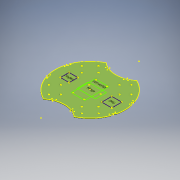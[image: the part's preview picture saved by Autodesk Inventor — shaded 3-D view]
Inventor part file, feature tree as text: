
AUTODESK INVENTOR PART (.ipt)
format: ipt  version: 2020 (Build 240168000, 168)  size: 317,952 bytes
history: native  units: mm
features: sketch x7, other x4, hole x4, extrude x2, fillet x1, projected_geometry x1
ambient origin geometry x8: Origin, YZ Plane, XZ Plane, XY Plane, X Axis, Y Axis, Z Axis, Center Point
bodies: Body1 (feature_tree)
feature tree (19):
  other  "motherboard"
  other  "contour"
  other  "Твердое тело1"
  extrude  "Выдавливание1"  Depth=10.0mm
  hole  "Отверстие1"  [1 undecoded]
  fillet  "Сопряжение1"  Radius=2.0mm
  hole  "Отверстие2"  [1 undecoded]
  sketch  "Эскиз7"
  extrude  "Выдавливание2"  Depth=62.0mm
  hole  "Отверстие3"  [1 undecoded]
  hole  "Отверстие4"  [1 undecoded]
  sketch  "Эскиз10"
  sketch  "Эскиз2"
  sketch  "Эскиз3"
  other  "Эскиз3_1"
  sketch  "Эскиз5"
  sketch  "Эскиз8"
  sketch  "Эскиз9"
  projected_geometry  "Спроецированная петля1"
note: 4 required parameter values undecoded (feature->parameter linkage not recoverable at this tier; creation-order binding heuristic only, values carry confidence <= 0.55)
